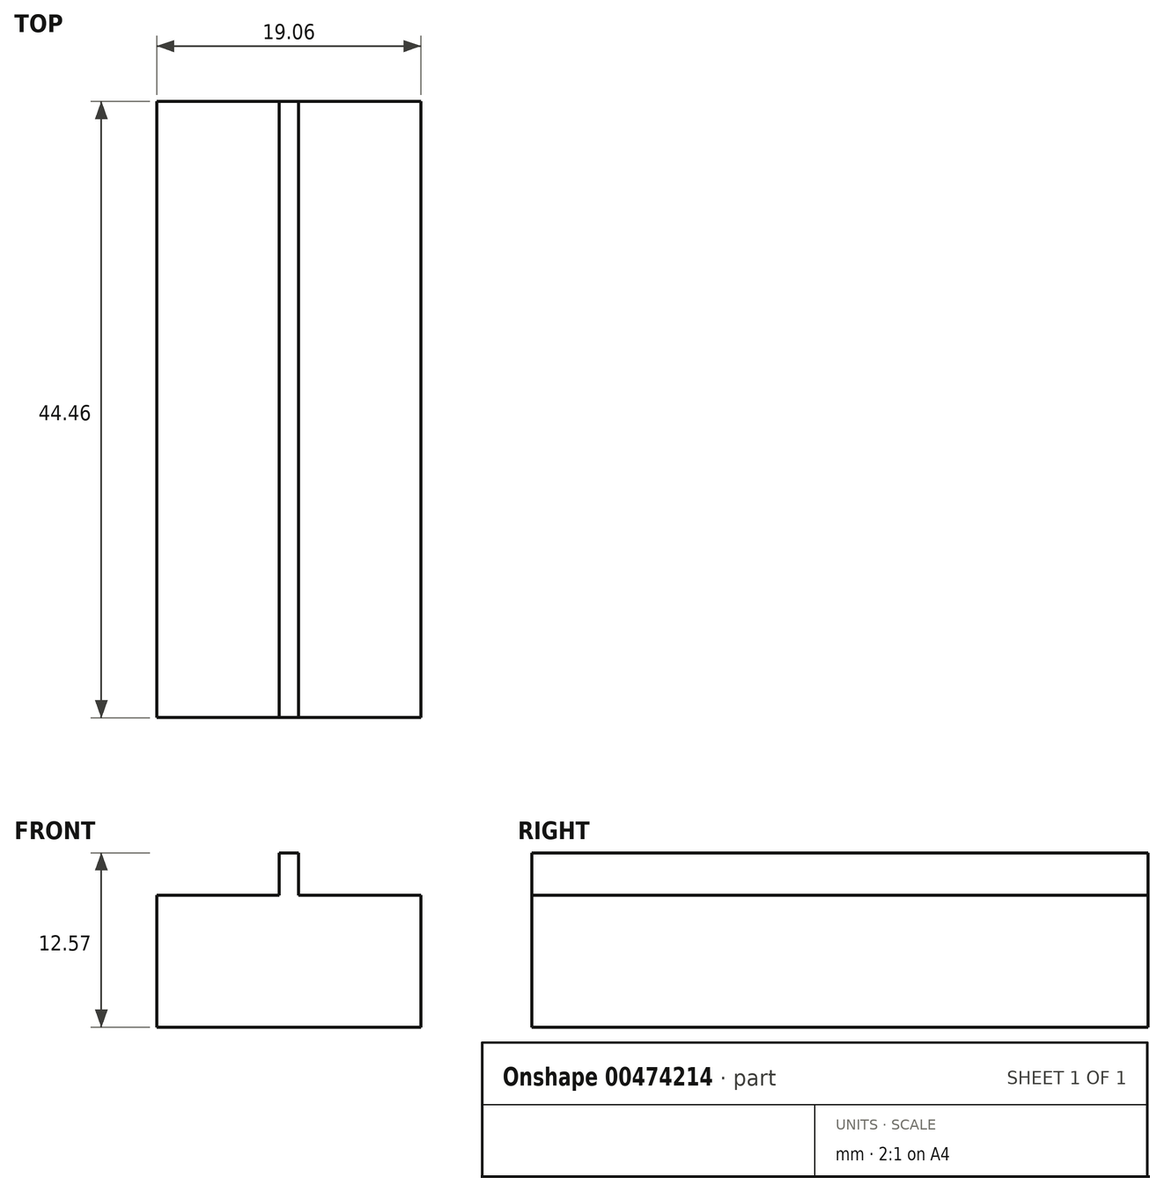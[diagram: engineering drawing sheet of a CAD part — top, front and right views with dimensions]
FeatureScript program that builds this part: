
annotation { "Feature Type Name" : "Feature", "Feature Type Description" : "" }
export const myFeature = defineFeature(function(context is Context, id is Id, definition is map)
    precondition{}
    {
        {
            var Q0;
            Q0=qCreatedBy(makeId("Top.planeOp"),FACE);
            var sketch = newSketch(context, id + "F0", { "sketchPlane" : qUnion([Q0])});
            skLineSegment(sketch, "E0.bottom", {"start": v(-9.52, 22.23) * mm, "end": v(9.52, 22.23) * mm});
            skLineSegment(sketch, "E0.top", {"start": v(-9.52, -22.23) * mm, "end": v(9.52, -22.23) * mm});
            skLineSegment(sketch, "E0.left", {"start": v(-9.53, 22.23) * mm, "end": v(-9.53, -22.23) * mm});
            skLineSegment(sketch, "E0.right", {"start": v(9.52, 22.23) * mm, "end": v(9.53, -22.23) * mm});
            skLineSegment(sketch, "E1", {"start": v(0, 22.23) * mm, "end": v(0, -22.23) * mm, "construction": true});
            skSolve(sketch);
        }
        {
            var Q0;
            Q0=makeQuery(id+"F0.imprint","IMPRINT",FACE,{"disambiguationData":[TD([[makeQuery(id+"F0.imprint","IMPRINT",EDGE,{"derivedFrom":sQuery(id+"F0.wireOp",EDGE,"E0.bottom")}),-1.0]])]});
            extrude(context, id + "F1", {"entities" : qUnion([Q0]), "depth" : 9.52 * mm});
        }
        {
            var Q0;
            Q0=makeQuery(id+"F1.opExtrude","CAP_FACE",FACE,{"disambiguationData":[OSD([sQuery(id+"F0.wireOp",EDGE,"E0.bottom"),sQuery(id+"F0.wireOp",EDGE,"E0.top"),sQuery(id+"F0.wireOp",EDGE,"E0.left"),sQuery(id+"F0.wireOp",EDGE,"E0.right")])],"isStart":false});
            var sketch = newSketch(context, id + "F2", { "sketchPlane" : qUnion([Q0])});
            skLineSegment(sketch, "E2", {"start": v(0, 22.23) * mm, "end": v(0, -22.23) * mm, "construction": true});
            skLineSegment(sketch, "E3.0", {"start": v(-0.71, 22.23) * mm, "end": v(-0.71, -22.23) * mm});
            skLineSegment(sketch, "E4.0", {"start": v(0.71, 22.23) * mm, "end": v(0.71, -22.23) * mm});
            skLineSegment(sketch, "E5", {"start": v(-0.71, 22.23) * mm, "end": v(0.71, 22.23) * mm});
            skLineSegment(sketch, "E6", {"start": v(-0.71, -22.23) * mm, "end": v(0.71, -22.23) * mm});
            skSolve(sketch);
        }
        {
            var Q0;
            Q0=makeQuery(id+"F2.imprint","IMPRINT",FACE,{"disambiguationData":[TD([[makeQuery(id+"F2.imprint","IMPRINT",EDGE,{"derivedFrom":sQuery(id+"F2.wireOp",EDGE,"E3.0")}),1.0]])]});
            extrude(context, id + "F3", {"entities" : qUnion([Q0]), "operationType" : NewBodyOperationType.ADD, "depth" : 3.05 * mm});
        }
    });
